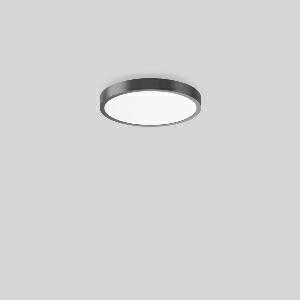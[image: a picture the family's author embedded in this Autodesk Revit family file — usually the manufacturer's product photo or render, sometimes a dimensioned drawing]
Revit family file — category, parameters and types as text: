
# Revit family: triona_round_a_312419_0031_1_730_c947
name_source: partatom
category: Lighting Fixtures
units: mm (PartAtom-declared; Revit-internal decimal feet)

## family parameters
Cut with Voids When Loaded = No
Host = Face
Light Source = No
Part Type = Normal
Room Calculation Point = No
Round Connector Dimension = Use Diameter
Shared = No

## types (1)
- TRIONA round A (1 x LED Modul 840, 4900 lm, 4000)
    Apparent Load = 48 VA
    CIE Flux Codes = 49 80 96 100 100
    Color Rendering = 80
    Color Temperature = 4000
    Default Elevation = 1800 mm
    Description = Series: TRIONA round
Decorative round LED surface-mounted luminaire. Flat, seamless frame: aluminium extrusion profile, powder coated. Cover made of sheet steel, powder-coated. Light emission through a diffuser: plastic, opal. Lightguide and diffuser made of non-yellowing plastic (PMMA). Lateral light emission (RZB SIDELITE technology) for above-average homogeneous light distribution. Suitable for Ceiling mounting, Wall (surface). Tool-free mounting via bayonet connection. Electronic ballast included. Very easy installation thanks to Plug+Play connection. With Casambi smart+free Bluetooth control for wireless network and operation using Android / iOS devices, free app available for download. 
Colour: anthracite metallic (DB703)
Diameter: 461 mm
Height: 88 mm
Lamp: LED
Socket: without socket
Colour temperature: 4000K
Colour rendering index (CRI): 80
System power: 48 W
Rated luminous flux: 4900 lm
Luminous efficiency: 102 lm/W
Control gear: Dimmable Bluetooth converter
Protection class: I
Type of protection: IP 20
    Height = 88 mm
    Lamp = 1 x LED Modul 840
    Lamp Light Flux = 4900 lm
    Lamp count = 1
    Length = 461 mm
    Lifetime = 50000 h
    Luminous efficacy = 102 lm/W
    Manufacturer = RZB
    ModVariant = No
    Model = 312419.0031.1.730
    Mounting Place = Ceiling
    Mounting Type = Surface mounted
    Number of Poles = 1
    OnlyDefault = Yes
    Power Factor = 1
    Product Name = TRIONA round A
    Product group = Surface mounted modular luminaires
    ProductGroupID = 306
    Protection Class = Protection class I
    Protection Degree = IP 20
    RLX_Detail_Level = 1
    RLX_Emergency_Light_Flux = 0 lm
    RLX_Emergency_Type = 0
    RLX_Emergency_Type_DB = No
    RlxData = <blob elided: 29213 chars, md5=bc4b43ea>
    Socket = socket
    Standby Power = 0 W
    System Light Flux = 4900 lm
    System Power = 48 W
    Type Comments = Product without accessories
    Type Image = 312420.0031.jpg
    URL = http://relux.com
    VarID = ---
    Voltage = 230 V
    Voltage Range = 220-240 V
    Weight = 0.00 kg
    Width = 0 mm  [stored 0 ft]

note: [stored X ft] marks values corroborated as IEEE doubles in the binary element streams (Revit-internal decimal feet)

## geometry (parser evidence)
native form markers: Blend x4, Sweep x10
no freeform markers — native parametric forms only
